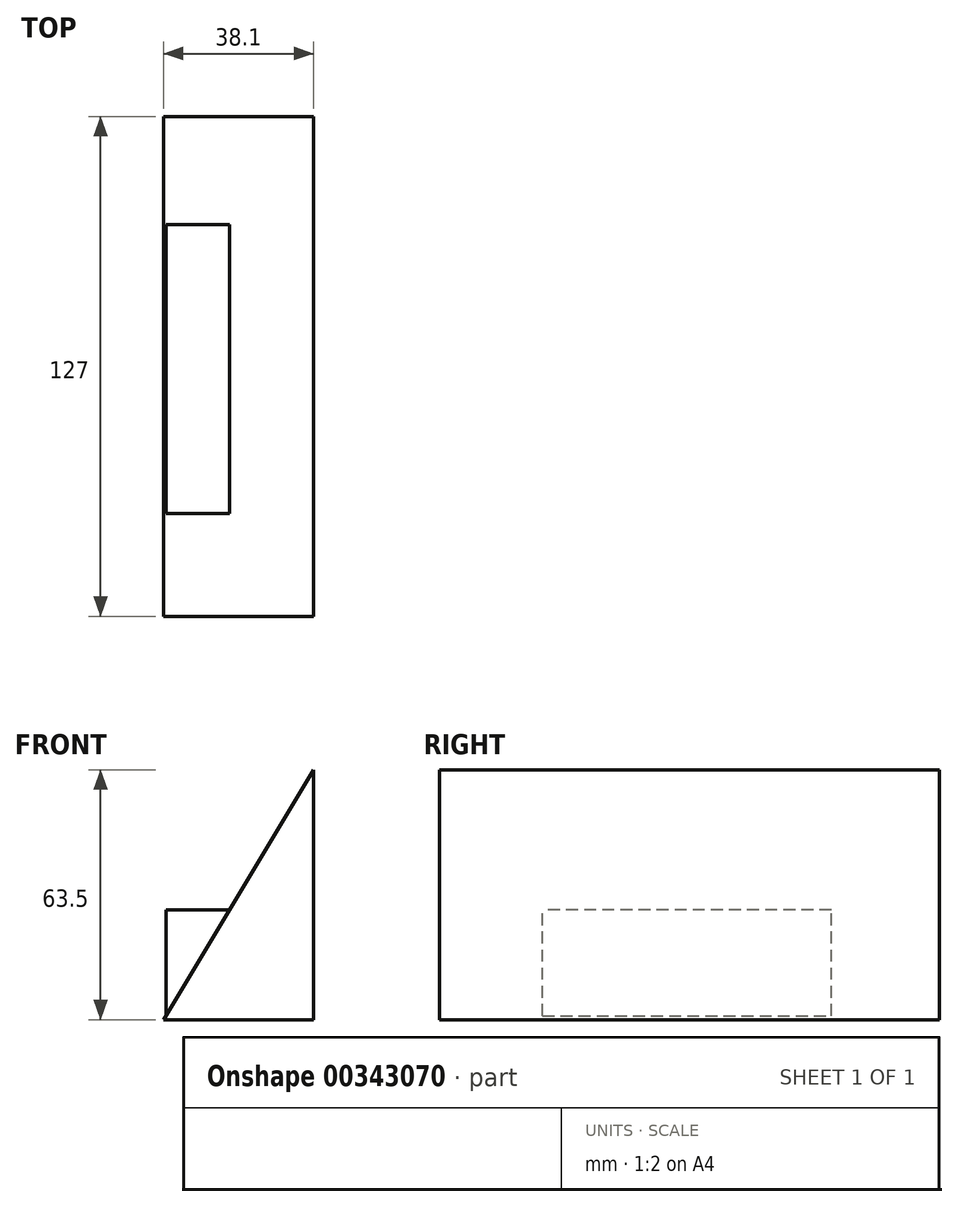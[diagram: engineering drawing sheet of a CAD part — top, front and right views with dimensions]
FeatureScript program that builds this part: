
annotation { "Feature Type Name" : "Feature", "Feature Type Description" : "" }
export const myFeature = defineFeature(function(context is Context, id is Id, definition is map)
    precondition{}
    {
        {
            var Q0;
            Q0=qCreatedBy(makeId("Front.planeOp"),FACE);
            var sketch = newSketch(context, id + "F0", { "sketchPlane" : qUnion([Q0])});
            skLineSegment(sketch, "E0", {"start": v(11.58, 23.71) * mm, "end": v(11.58, -39.79) * mm});
            skLineSegment(sketch, "E1", {"start": v(11.58, -39.79) * mm, "end": v(-26.52, -39.79) * mm});
            skLineSegment(sketch, "E2", {"start": v(-26.52, -39.79) * mm, "end": v(11.58, 23.71) * mm});
            skSolve(sketch);
        }
        {
            var Q0;
            Q0 = qSketchRegion(id + "F0", true);
            extrude(context, id + "F1", {"entities" : qUnion([Q0]), "depth" : 127 * mm});
        }
        {
            var Q0;
            Q0=qCreatedBy(makeId("Front.planeOp"),FACE);
            var sketch = newSketch(context, id + "F2", { "sketchPlane" : qUnion([Q0])});
            skLineSegment(sketch, "E3", {"start": v(-25.94, -39.2) * mm, "end": v(-9.76, -11.89) * mm});
            skLineSegment(sketch, "E4", {"start": v(-9.76, -11.89) * mm, "end": v(-25.94, -11.89) * mm});
            skLineSegment(sketch, "E5", {"start": v(-25.94, -11.89) * mm, "end": v(-25.94, -39.2) * mm});
            skSolve(sketch);
        }
        {
            var Q0;
            Q0 = qSketchRegion(id + "F2", true);
            extrude(context, id + "F3", {"entities" : qUnion([Q0]), "operationType" : NewBodyOperationType.ADD, "depth" : 100.84 * mm, "hasSecondDirection" : true, "secondDirectionOppositeDirection" : false, "secondDirectionDepth" : 27.43 * mm});
        }
    });
